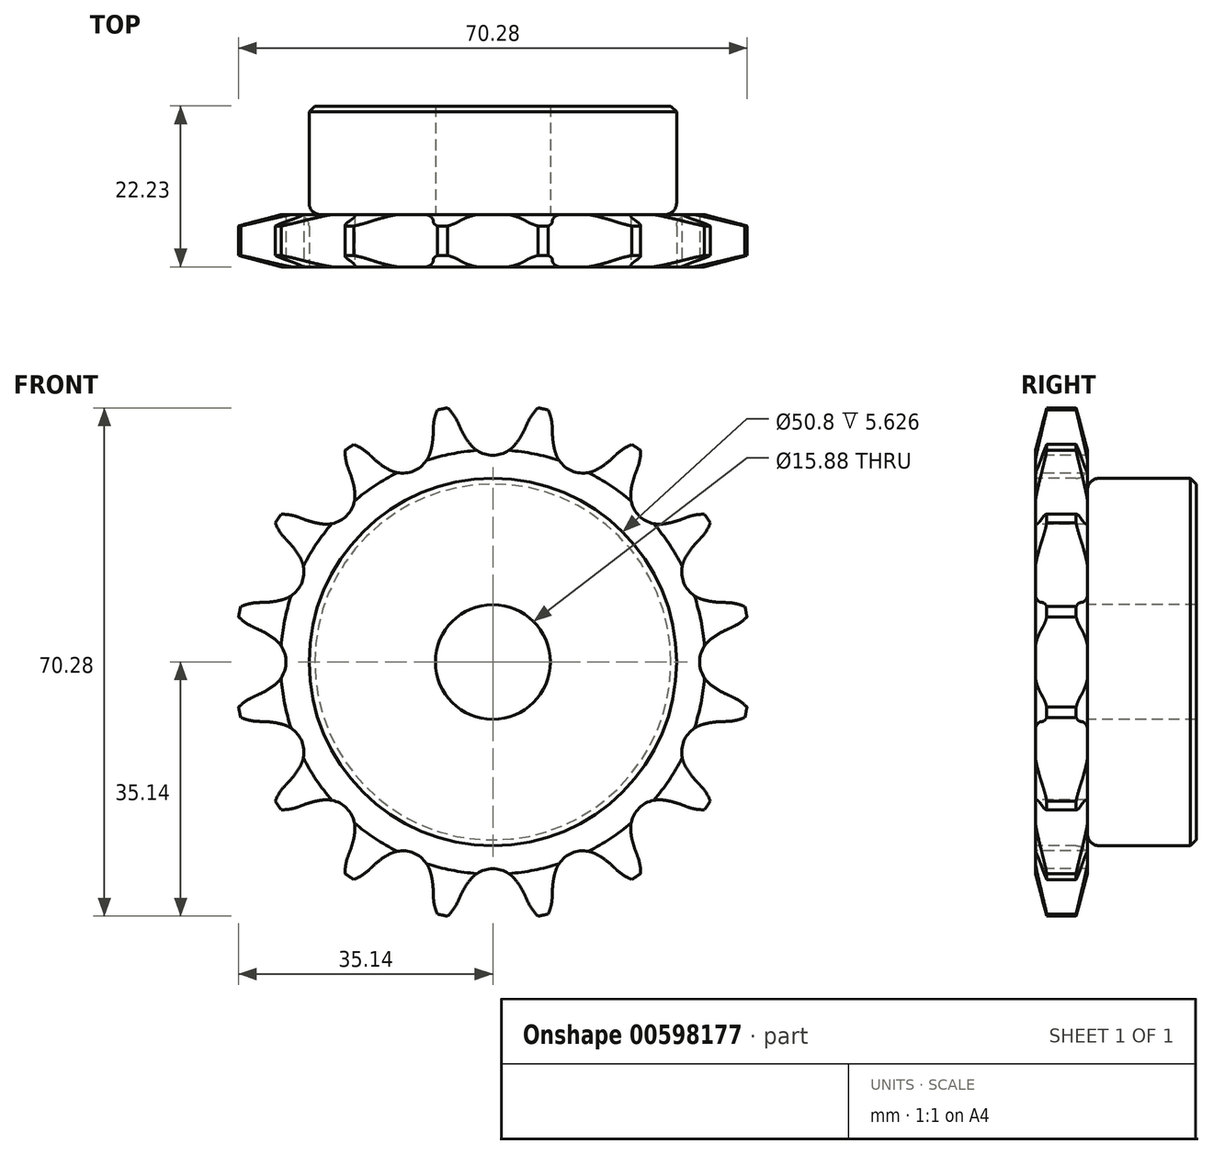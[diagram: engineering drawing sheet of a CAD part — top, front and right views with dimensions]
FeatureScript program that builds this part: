
annotation { "Feature Type Name" : "Feature", "Feature Type Description" : "" }
export const myFeature = defineFeature(function(context is Context, id is Id, definition is map)
    precondition{}
    {
        {
            var Q0;
            Q0=qCreatedBy(makeId("Right.planeOp"),FACE);
            var sketch = newSketch(context, id + "F0", { "sketchPlane" : qUnion([Q0])});
            skLineSegment(sketch, "E0", {"start": v(0, 0) * mm, "end": v(22.23, 0) * mm, "construction": true});
            skLineSegment(sketch, "E1.bottom", {"start": v(0, 7.94) * mm, "end": v(7.21, 7.94) * mm});
            skLineSegment(sketch, "E1.top", {"start": v(0, 35.69) * mm, "end": v(7.21, 35.69) * mm});
            skLineSegment(sketch, "E1.left", {"start": v(0, 7.94) * mm, "end": v(0, 35.69) * mm});
            skLineSegment(sketch, "E1.right", {"start": v(7.21, 7.94) * mm, "end": v(7.21, 35.69) * mm});
            skLineSegment(sketch, "E2.bottom", {"start": v(0, 7.94) * mm, "end": v(22.23, 7.94) * mm});
            skLineSegment(sketch, "E2.top", {"start": v(0, 25.4) * mm, "end": v(22.23, 25.4) * mm});
            skLineSegment(sketch, "E2.left", {"start": v(0, 7.94) * mm, "end": v(0, 25.4) * mm});
            skLineSegment(sketch, "E2.right", {"start": v(22.23, 7.94) * mm, "end": v(22.22, 25.4) * mm});
            skLineSegment(sketch, "E3.MirrorCS", {"start": v(0, -7.94) * mm, "end": v(7.21, -7.94) * mm});
            skLineSegment(sketch, "E4.MirrorCS", {"start": v(22.23, -7.94) * mm, "end": v(22.23, -25.4) * mm});
            skLineSegment(sketch, "E5.MirrorCS", {"start": v(0, -7.94) * mm, "end": v(0, -25.4) * mm});
            skLineSegment(sketch, "E6.MirrorCS", {"start": v(0, -35.69) * mm, "end": v(7.21, -35.69) * mm});
            skLineSegment(sketch, "E7.MirrorCS", {"start": v(0, -7.94) * mm, "end": v(0, -35.69) * mm});
            skLineSegment(sketch, "E8.MirrorCS", {"start": v(7.21, -7.94) * mm, "end": v(7.21, -35.69) * mm});
            skLineSegment(sketch, "E9.MirrorCS", {"start": v(0, -7.94) * mm, "end": v(22.23, -7.94) * mm});
            skLineSegment(sketch, "E10.MirrorCS", {"start": v(0, -25.4) * mm, "end": v(22.23, -25.4) * mm});
            skSolve(sketch);
        }
        {
            var Q0;
            {var subQ0=sQuery(id+"F0.wireOp",EDGE,"E1.top");Q0=makeQuery(id+"F0.imprint","IMPRINT",FACE,{"disambiguationData":[TD([[makeQuery(id+"F0.imprint","IMPRINT",EDGE,{"derivedFrom":subQ0}),-1.0]])]});}
            var Q1;
            {var subQ5=sQuery(id+"F0.wireOp",EDGE,"E2.left");Q1=makeQuery(id+"F0.imprint","IMPRINT",FACE,{"disambiguationData":[TD([[makeQuery(id+"F0.imprint","IMPRINT",EDGE,{"derivedFrom":subQ5}),-1.0]])]});}
            var Q2;
            {var subQ5=sQuery(id+"F0.wireOp",EDGE,"E2.right");Q2=makeQuery(id+"F0.imprint","IMPRINT",FACE,{"disambiguationData":[TD([[makeQuery(id+"F0.imprint","IMPRINT",EDGE,{"derivedFrom":subQ5}),1.0]])]});}
            var Q3;
            Q3=sQuery(id+"F0.wireOp",EDGE,"E0");
            revolve(context, id + "F1", {"entities" : qUnion([Q0, Q1, Q2]), "axis" : qUnion([Q3]), "revolveType" : RevolveType.FULL});
        }
        {
            var Q0;
            Q0=makeQuery(id+"F1.opRevolve","SWEPT_EDGE",EDGE,{"disambiguationData":[OSD([sQuery(id+"F0.wireOp",EDGE,"E1.right"),sQuery(id+"F0.wireOp",EDGE,"E2.top")])]});
            fillet(context, id + "F2", {"entities" : qUnion([Q0]), "radius" : 1.59 * mm, "tangentPropagation" : true, "allowEdgeOverflow" : false});
        }
        {
            var Q0;
            Q0=makeQuery(id+"F1.opRevolve","SWEPT_EDGE",EDGE,{"disambiguationData":[OSD([sQuery(id+"F0.wireOp",EDGE,"E2.top"),sQuery(id+"F0.wireOp",EDGE,"E2.right")])]});
            chamfer(context, id + "F3", {"entities" : qUnion([Q0]), "width" : 0.8 * mm, "tangentPropagation" : true});
        }
        {
            var Q0;
            Q0=makeQuery(id+"F1.opRevolve","SWEPT_EDGE",EDGE,{"disambiguationData":[OSD([sQuery(id+"F0.wireOp",EDGE,"E1.top"),sQuery(id+"F0.wireOp",EDGE,"E1.left")])]});
            var Q1;
            Q1=makeQuery(id+"F1.opRevolve","SWEPT_EDGE",EDGE,{"disambiguationData":[OSD([sQuery(id+"F0.wireOp",EDGE,"E1.top"),sQuery(id+"F0.wireOp",EDGE,"E1.right")])]});
            chamfer(context, id + "F4", {"entities" : qUnion([Q0, Q1]), "chamferType" : ChamferType.TWO_OFFSETS, "width1" : 6.35 * mm, "oppositeDirection" : false, "width2" : 1.57 * mm, "tangentPropagation" : true});
        }
        {
            var Q0;
            Q0=qCreatedBy(makeId("Front.planeOp"),FACE);
            var sketch = newSketch(context, id + "F5", { "sketchPlane" : qUnion([Q0])});
            skCircle(sketch, "E11", {"center": v(0, 0) * mm, "radius": 32.55 * mm, "construction": true});
            skLineSegment(sketch, "E12", {"start": v(0, 0) * mm, "end": v(0, 32.55) * mm, "construction": true});
            skLineSegment(sketch, "E13", {"start": v(0, 32.55) * mm, "end": v(73.94, 32.55) * mm, "construction": true});
            skLineSegment(sketch, "E14", {"start": v(0, 32.55) * mm, "end": v(5, 36.56) * mm, "construction": true});
            skLineSegment(sketch, "E15", {"start": v(5, 36.56) * mm, "end": v(-4.46, 32.3) * mm, "construction": true});
            skLineSegment(sketch, "E16", {"start": v(-4.46, 32.3) * mm, "end": v(-4.82, 33.1) * mm});
            skLineSegment(sketch, "E17", {"start": v(0, 0) * mm, "end": v(-7.13, 35.85) * mm, "construction": true});
            skArc(sketch, "E18", {"start": v(-7.13, 35.85) * mm, "mid": v(-15.87, 26.15) * mm, "end": v(-4.82, 33.1) * mm, "construction": true});
            skArc(sketch, "E19", {"start": v(-4.82, 33.1) * mm, "mid": v(-5.78, 34.63) * mm, "end": v(-7.13, 35.85) * mm});
            skArc(sketch, "E20", {"start": v(-4.46, 32.3) * mm, "mid": v(-3.84, 31.14) * mm, "end": v(-3.1, 30.07) * mm});
            skArc(sketch, "E21", {"start": v(-3.1, 30.07) * mm, "mid": v(13.83, 41.97) * mm, "end": v(-4.46, 32.3) * mm, "construction": true});
            skArc(sketch, "E22.0.MirrorCS", {"start": v(4.46, 32.3) * mm, "mid": v(3.84, 31.14) * mm, "end": v(3.1, 30.07) * mm});
            skLineSegment(sketch, "E23.0.MirrorCS", {"start": v(4.46, 32.3) * mm, "end": v(4.82, 33.1) * mm});
            skArc(sketch, "E24.0.MirrorCS", {"start": v(4.82, 33.1) * mm, "mid": v(5.78, 34.63) * mm, "end": v(7.13, 35.85) * mm});
            skArc(sketch, "E25", {"start": v(-3.1, 30.07) * mm, "mid": v(0, 28.59) * mm, "end": v(3.1, 30.07) * mm});
            skArc(sketch, "E26", {"start": v(3.1, 30.07) * mm, "mid": v(0, 36.51) * mm, "end": v(-3.1, 30.07) * mm, "construction": true});
            skArc(sketch, "E27.1.0", {"start": v(-17.12, 28.74) * mm, "mid": v(-18.6, 29.79) * mm, "end": v(-20.3, 30.4) * mm});
            skLineSegment(sketch, "E27.1.1", {"start": v(-16.48, 28.14) * mm, "end": v(-17.12, 28.74) * mm});
            skArc(sketch, "E27.1.2", {"start": v(-16.48, 28.14) * mm, "mid": v(-15.47, 27.3) * mm, "end": v(-14.36, 26.6) * mm});
            skArc(sketch, "E27.1.3", {"start": v(-14.36, 26.6) * mm, "mid": v(-10.94, 26.41) * mm, "end": v(-8.65, 28.96) * mm});
            skArc(sketch, "E27.1.4", {"start": v(-8.24, 31.55) * mm, "mid": v(-8.37, 30.24) * mm, "end": v(-8.65, 28.96) * mm});
            skLineSegment(sketch, "E27.1.5", {"start": v(-8.24, 31.55) * mm, "end": v(-8.22, 32.42) * mm});
            skArc(sketch, "E27.1.6", {"start": v(-8.22, 32.42) * mm, "mid": v(-7.91, 34.21) * mm, "end": v(-7.13, 35.85) * mm});
            skArc(sketch, "E27.2.0", {"start": v(-26.8, 20) * mm, "mid": v(-28.58, 20.4) * mm, "end": v(-30.4, 20.3) * mm});
            skLineSegment(sketch, "E27.2.1", {"start": v(-26, 19.69) * mm, "end": v(-26.8, 20) * mm});
            skArc(sketch, "E27.2.2", {"start": v(-26, 19.69) * mm, "mid": v(-24.74, 19.3) * mm, "end": v(-23.45, 19.08) * mm});
            skArc(sketch, "E27.2.3", {"start": v(-23.45, 19.08) * mm, "mid": v(-20.21, 20.21) * mm, "end": v(-19.08, 23.45) * mm});
            skArc(sketch, "E27.2.4", {"start": v(-19.69, 26) * mm, "mid": v(-19.3, 24.74) * mm, "end": v(-19.08, 23.45) * mm});
            skLineSegment(sketch, "E27.2.5", {"start": v(-19.69, 26) * mm, "end": v(-20, 26.8) * mm});
            skArc(sketch, "E27.2.6", {"start": v(-20, 26.8) * mm, "mid": v(-20.4, 28.58) * mm, "end": v(-20.3, 30.4) * mm});
            skArc(sketch, "E27.3.0", {"start": v(-32.42, 8.22) * mm, "mid": v(-34.21, 7.91) * mm, "end": v(-35.85, 7.13) * mm});
            skLineSegment(sketch, "E27.3.1", {"start": v(-31.55, 8.24) * mm, "end": v(-32.42, 8.22) * mm});
            skArc(sketch, "E27.3.2", {"start": v(-31.55, 8.24) * mm, "mid": v(-30.24, 8.37) * mm, "end": v(-28.96, 8.65) * mm});
            skArc(sketch, "E27.3.3", {"start": v(-28.96, 8.65) * mm, "mid": v(-26.41, 10.94) * mm, "end": v(-26.6, 14.36) * mm});
            skArc(sketch, "E27.3.4", {"start": v(-28.14, 16.48) * mm, "mid": v(-27.3, 15.47) * mm, "end": v(-26.6, 14.36) * mm});
            skLineSegment(sketch, "E27.3.5", {"start": v(-28.14, 16.48) * mm, "end": v(-28.74, 17.12) * mm});
            skArc(sketch, "E27.3.6", {"start": v(-28.74, 17.12) * mm, "mid": v(-29.79, 18.6) * mm, "end": v(-30.4, 20.3) * mm});
            skArc(sketch, "E27.4.0", {"start": v(-33.1, -4.82) * mm, "mid": v(-34.63, -5.78) * mm, "end": v(-35.85, -7.13) * mm});
            skLineSegment(sketch, "E27.4.1", {"start": v(-32.3, -4.46) * mm, "end": v(-33.1, -4.82) * mm});
            skArc(sketch, "E27.4.2", {"start": v(-32.3, -4.46) * mm, "mid": v(-31.14, -3.84) * mm, "end": v(-30.07, -3.1) * mm});
            skArc(sketch, "E27.4.3", {"start": v(-30.07, -3.1) * mm, "mid": v(-28.59, 0) * mm, "end": v(-30.07, 3.1) * mm});
            skArc(sketch, "E27.4.4", {"start": v(-32.3, 4.46) * mm, "mid": v(-31.14, 3.84) * mm, "end": v(-30.07, 3.1) * mm});
            skLineSegment(sketch, "E27.4.5", {"start": v(-32.3, 4.46) * mm, "end": v(-33.1, 4.82) * mm});
            skArc(sketch, "E27.4.6", {"start": v(-33.1, 4.82) * mm, "mid": v(-34.63, 5.78) * mm, "end": v(-35.85, 7.13) * mm});
            skArc(sketch, "E27.5.0", {"start": v(-28.74, -17.12) * mm, "mid": v(-29.79, -18.6) * mm, "end": v(-30.4, -20.3) * mm});
            skLineSegment(sketch, "E27.5.1", {"start": v(-28.14, -16.48) * mm, "end": v(-28.74, -17.12) * mm});
            skArc(sketch, "E27.5.2", {"start": v(-28.14, -16.48) * mm, "mid": v(-27.3, -15.47) * mm, "end": v(-26.6, -14.36) * mm});
            skArc(sketch, "E27.5.3", {"start": v(-26.6, -14.36) * mm, "mid": v(-26.41, -10.94) * mm, "end": v(-28.96, -8.65) * mm});
            skArc(sketch, "E27.5.4", {"start": v(-31.55, -8.24) * mm, "mid": v(-30.24, -8.37) * mm, "end": v(-28.96, -8.65) * mm});
            skLineSegment(sketch, "E27.5.5", {"start": v(-31.55, -8.24) * mm, "end": v(-32.42, -8.22) * mm});
            skArc(sketch, "E27.5.6", {"start": v(-32.42, -8.22) * mm, "mid": v(-34.21, -7.91) * mm, "end": v(-35.85, -7.13) * mm});
            skArc(sketch, "E27.6.0", {"start": v(-20, -26.8) * mm, "mid": v(-20.4, -28.58) * mm, "end": v(-20.3, -30.4) * mm});
            skLineSegment(sketch, "E27.6.1", {"start": v(-19.69, -26) * mm, "end": v(-20, -26.8) * mm});
            skArc(sketch, "E27.6.2", {"start": v(-19.69, -26) * mm, "mid": v(-19.3, -24.74) * mm, "end": v(-19.08, -23.45) * mm});
            skArc(sketch, "E27.6.3", {"start": v(-19.08, -23.45) * mm, "mid": v(-20.21, -20.21) * mm, "end": v(-23.45, -19.08) * mm});
            skArc(sketch, "E27.6.4", {"start": v(-26, -19.69) * mm, "mid": v(-24.74, -19.3) * mm, "end": v(-23.45, -19.08) * mm});
            skLineSegment(sketch, "E27.6.5", {"start": v(-26, -19.69) * mm, "end": v(-26.8, -20) * mm});
            skArc(sketch, "E27.6.6", {"start": v(-26.8, -20) * mm, "mid": v(-28.58, -20.4) * mm, "end": v(-30.4, -20.3) * mm});
            skArc(sketch, "E27.7.0", {"start": v(-8.22, -32.42) * mm, "mid": v(-7.91, -34.21) * mm, "end": v(-7.13, -35.85) * mm});
            skLineSegment(sketch, "E27.7.1", {"start": v(-8.24, -31.55) * mm, "end": v(-8.22, -32.42) * mm});
            skArc(sketch, "E27.7.2", {"start": v(-8.24, -31.55) * mm, "mid": v(-8.37, -30.24) * mm, "end": v(-8.65, -28.96) * mm});
            skArc(sketch, "E27.7.3", {"start": v(-8.65, -28.96) * mm, "mid": v(-10.94, -26.41) * mm, "end": v(-14.36, -26.6) * mm});
            skArc(sketch, "E27.7.4", {"start": v(-16.48, -28.14) * mm, "mid": v(-15.47, -27.3) * mm, "end": v(-14.36, -26.6) * mm});
            skLineSegment(sketch, "E27.7.5", {"start": v(-16.48, -28.14) * mm, "end": v(-17.12, -28.74) * mm});
            skArc(sketch, "E27.7.6", {"start": v(-17.12, -28.74) * mm, "mid": v(-18.6, -29.79) * mm, "end": v(-20.3, -30.4) * mm});
            skArc(sketch, "E27.8.0", {"start": v(4.82, -33.1) * mm, "mid": v(5.78, -34.63) * mm, "end": v(7.13, -35.85) * mm});
            skLineSegment(sketch, "E27.8.1", {"start": v(4.46, -32.3) * mm, "end": v(4.82, -33.1) * mm});
            skArc(sketch, "E27.8.2", {"start": v(4.46, -32.3) * mm, "mid": v(3.84, -31.14) * mm, "end": v(3.1, -30.07) * mm});
            skArc(sketch, "E27.8.3", {"start": v(3.1, -30.07) * mm, "mid": v(0, -28.59) * mm, "end": v(-3.1, -30.07) * mm});
            skArc(sketch, "E27.8.4", {"start": v(-4.46, -32.3) * mm, "mid": v(-3.84, -31.14) * mm, "end": v(-3.1, -30.07) * mm});
            skLineSegment(sketch, "E27.8.5", {"start": v(-4.46, -32.3) * mm, "end": v(-4.82, -33.1) * mm});
            skArc(sketch, "E27.8.6", {"start": v(-4.82, -33.1) * mm, "mid": v(-5.78, -34.63) * mm, "end": v(-7.13, -35.85) * mm});
            skArc(sketch, "E27.9.0", {"start": v(17.12, -28.74) * mm, "mid": v(18.6, -29.79) * mm, "end": v(20.3, -30.4) * mm});
            skLineSegment(sketch, "E27.9.1", {"start": v(16.48, -28.14) * mm, "end": v(17.12, -28.74) * mm});
            skArc(sketch, "E27.9.2", {"start": v(16.48, -28.14) * mm, "mid": v(15.47, -27.3) * mm, "end": v(14.36, -26.6) * mm});
            skArc(sketch, "E27.9.3", {"start": v(14.36, -26.6) * mm, "mid": v(10.94, -26.41) * mm, "end": v(8.65, -28.96) * mm});
            skArc(sketch, "E27.9.4", {"start": v(8.24, -31.55) * mm, "mid": v(8.37, -30.24) * mm, "end": v(8.65, -28.96) * mm});
            skLineSegment(sketch, "E27.9.5", {"start": v(8.24, -31.55) * mm, "end": v(8.22, -32.42) * mm});
            skArc(sketch, "E27.9.6", {"start": v(8.22, -32.42) * mm, "mid": v(7.91, -34.21) * mm, "end": v(7.13, -35.85) * mm});
            skArc(sketch, "E27.10.0", {"start": v(26.8, -20) * mm, "mid": v(28.58, -20.4) * mm, "end": v(30.4, -20.3) * mm});
            skLineSegment(sketch, "E27.10.1", {"start": v(26, -19.69) * mm, "end": v(26.8, -20) * mm});
            skArc(sketch, "E27.10.2", {"start": v(26, -19.69) * mm, "mid": v(24.74, -19.3) * mm, "end": v(23.45, -19.08) * mm});
            skArc(sketch, "E27.10.3", {"start": v(23.45, -19.08) * mm, "mid": v(20.21, -20.21) * mm, "end": v(19.08, -23.45) * mm});
            skArc(sketch, "E27.10.4", {"start": v(19.69, -26) * mm, "mid": v(19.3, -24.74) * mm, "end": v(19.08, -23.45) * mm});
            skLineSegment(sketch, "E27.10.5", {"start": v(19.69, -26) * mm, "end": v(20, -26.8) * mm});
            skArc(sketch, "E27.10.6", {"start": v(20, -26.8) * mm, "mid": v(20.4, -28.58) * mm, "end": v(20.3, -30.4) * mm});
            skArc(sketch, "E27.11.0", {"start": v(32.42, -8.22) * mm, "mid": v(34.21, -7.91) * mm, "end": v(35.85, -7.13) * mm});
            skLineSegment(sketch, "E27.11.1", {"start": v(31.55, -8.24) * mm, "end": v(32.42, -8.22) * mm});
            skArc(sketch, "E27.11.2", {"start": v(31.55, -8.24) * mm, "mid": v(30.24, -8.37) * mm, "end": v(28.96, -8.65) * mm});
            skArc(sketch, "E27.11.3", {"start": v(28.96, -8.65) * mm, "mid": v(26.41, -10.94) * mm, "end": v(26.6, -14.36) * mm});
            skArc(sketch, "E27.11.4", {"start": v(28.14, -16.48) * mm, "mid": v(27.3, -15.47) * mm, "end": v(26.6, -14.36) * mm});
            skLineSegment(sketch, "E27.11.5", {"start": v(28.14, -16.48) * mm, "end": v(28.74, -17.12) * mm});
            skArc(sketch, "E27.11.6", {"start": v(28.74, -17.12) * mm, "mid": v(29.79, -18.6) * mm, "end": v(30.4, -20.3) * mm});
            skArc(sketch, "E27.12.0", {"start": v(33.1, 4.82) * mm, "mid": v(34.63, 5.78) * mm, "end": v(35.85, 7.13) * mm});
            skLineSegment(sketch, "E27.12.1", {"start": v(32.3, 4.46) * mm, "end": v(33.1, 4.82) * mm});
            skArc(sketch, "E27.12.2", {"start": v(32.3, 4.46) * mm, "mid": v(31.14, 3.84) * mm, "end": v(30.07, 3.1) * mm});
            skArc(sketch, "E27.12.3", {"start": v(30.07, 3.1) * mm, "mid": v(28.59, 0) * mm, "end": v(30.07, -3.1) * mm});
            skArc(sketch, "E27.12.4", {"start": v(32.3, -4.46) * mm, "mid": v(31.14, -3.84) * mm, "end": v(30.07, -3.1) * mm});
            skLineSegment(sketch, "E27.12.5", {"start": v(32.3, -4.46) * mm, "end": v(33.1, -4.82) * mm});
            skArc(sketch, "E27.12.6", {"start": v(33.1, -4.82) * mm, "mid": v(34.63, -5.78) * mm, "end": v(35.85, -7.13) * mm});
            skArc(sketch, "E27.13.0", {"start": v(28.74, 17.12) * mm, "mid": v(29.79, 18.6) * mm, "end": v(30.4, 20.3) * mm});
            skLineSegment(sketch, "E27.13.1", {"start": v(28.14, 16.48) * mm, "end": v(28.74, 17.12) * mm});
            skArc(sketch, "E27.13.2", {"start": v(28.14, 16.48) * mm, "mid": v(27.3, 15.47) * mm, "end": v(26.6, 14.36) * mm});
            skArc(sketch, "E27.13.3", {"start": v(26.6, 14.36) * mm, "mid": v(26.41, 10.94) * mm, "end": v(28.96, 8.65) * mm});
            skArc(sketch, "E27.13.4", {"start": v(31.55, 8.24) * mm, "mid": v(30.24, 8.37) * mm, "end": v(28.96, 8.65) * mm});
            skLineSegment(sketch, "E27.13.5", {"start": v(31.55, 8.24) * mm, "end": v(32.42, 8.22) * mm});
            skArc(sketch, "E27.13.6", {"start": v(32.42, 8.22) * mm, "mid": v(34.21, 7.91) * mm, "end": v(35.85, 7.13) * mm});
            skArc(sketch, "E27.14.0", {"start": v(20, 26.8) * mm, "mid": v(20.4, 28.58) * mm, "end": v(20.3, 30.4) * mm});
            skLineSegment(sketch, "E27.14.1", {"start": v(19.69, 26) * mm, "end": v(20, 26.8) * mm});
            skArc(sketch, "E27.14.2", {"start": v(19.69, 26) * mm, "mid": v(19.3, 24.74) * mm, "end": v(19.08, 23.45) * mm});
            skArc(sketch, "E27.14.3", {"start": v(19.08, 23.45) * mm, "mid": v(20.21, 20.21) * mm, "end": v(23.45, 19.08) * mm});
            skArc(sketch, "E27.14.4", {"start": v(26, 19.69) * mm, "mid": v(24.74, 19.3) * mm, "end": v(23.45, 19.08) * mm});
            skLineSegment(sketch, "E27.14.5", {"start": v(26, 19.69) * mm, "end": v(26.8, 20) * mm});
            skArc(sketch, "E27.14.6", {"start": v(26.8, 20) * mm, "mid": v(28.58, 20.4) * mm, "end": v(30.4, 20.3) * mm});
            skArc(sketch, "E27.15.0", {"start": v(8.22, 32.42) * mm, "mid": v(7.91, 34.21) * mm, "end": v(7.13, 35.85) * mm});
            skLineSegment(sketch, "E27.15.1", {"start": v(8.24, 31.55) * mm, "end": v(8.22, 32.42) * mm});
            skArc(sketch, "E27.15.2", {"start": v(8.24, 31.55) * mm, "mid": v(8.37, 30.24) * mm, "end": v(8.65, 28.96) * mm});
            skArc(sketch, "E27.15.3", {"start": v(8.65, 28.96) * mm, "mid": v(10.94, 26.41) * mm, "end": v(14.36, 26.6) * mm});
            skArc(sketch, "E27.15.4", {"start": v(16.48, 28.14) * mm, "mid": v(15.47, 27.3) * mm, "end": v(14.36, 26.6) * mm});
            skLineSegment(sketch, "E27.15.5", {"start": v(16.48, 28.14) * mm, "end": v(17.12, 28.74) * mm});
            skArc(sketch, "E27.15.6", {"start": v(17.12, 28.74) * mm, "mid": v(18.6, 29.79) * mm, "end": v(20.3, 30.4) * mm});
            skSolve(sketch);
        }
        {
            var Q0;
            Q0 = qSketchRegion(id + "F5", true);
            extrude(context, id + "F6", {"entities" : qUnion([Q0]), "operationType" : NewBodyOperationType.INTERSECT, "endBound" : BoundingType.THROUGH_ALL, "oppositeDirection" : true, "depth" : 25.4 * mm, "offsetDistance" : 25.4 * mm});
        }
    });
